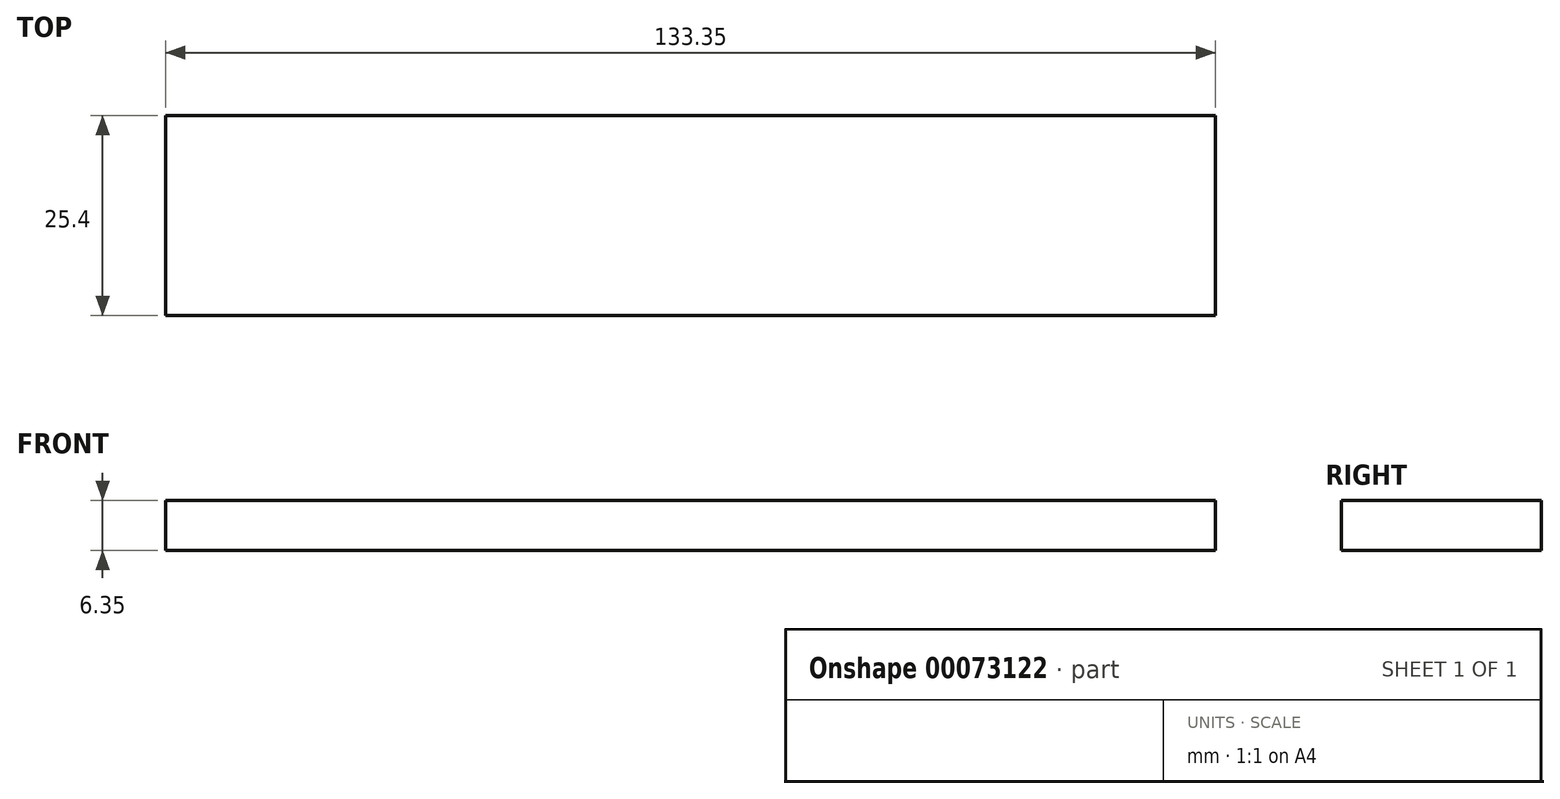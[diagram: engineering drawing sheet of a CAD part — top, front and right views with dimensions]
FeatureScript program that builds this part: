
annotation { "Feature Type Name" : "Feature", "Feature Type Description" : "" }
export const myFeature = defineFeature(function(context is Context, id is Id, definition is map)
    precondition{}
    {
        {
            var Q0;
            Q0=qCreatedBy(makeId("Top.planeOp"),FACE);
            var sketch = newSketch(context, id + "F0", { "sketchPlane" : qUnion([Q0])});
            skLineSegment(sketch, "E0.bottom", {"start": v(0, 0) * mm, "end": v(-133.35, 0) * mm});
            skLineSegment(sketch, "E0.top", {"start": v(0, 25.4) * mm, "end": v(-133.35, 25.4) * mm});
            skLineSegment(sketch, "E0.left", {"start": v(0, 0) * mm, "end": v(0, 25.4) * mm});
            skLineSegment(sketch, "E0.right", {"start": v(-133.35, 0) * mm, "end": v(-133.35, 25.4) * mm});
            skSolve(sketch);
        }
        {
            var Q0;
            Q0=qSketchRegion(id+"F0",true);
            extrude(context, id + "F1", {"entities" : qUnion([Q0]), "depth" : 6.35 * mm});
        }
    });
